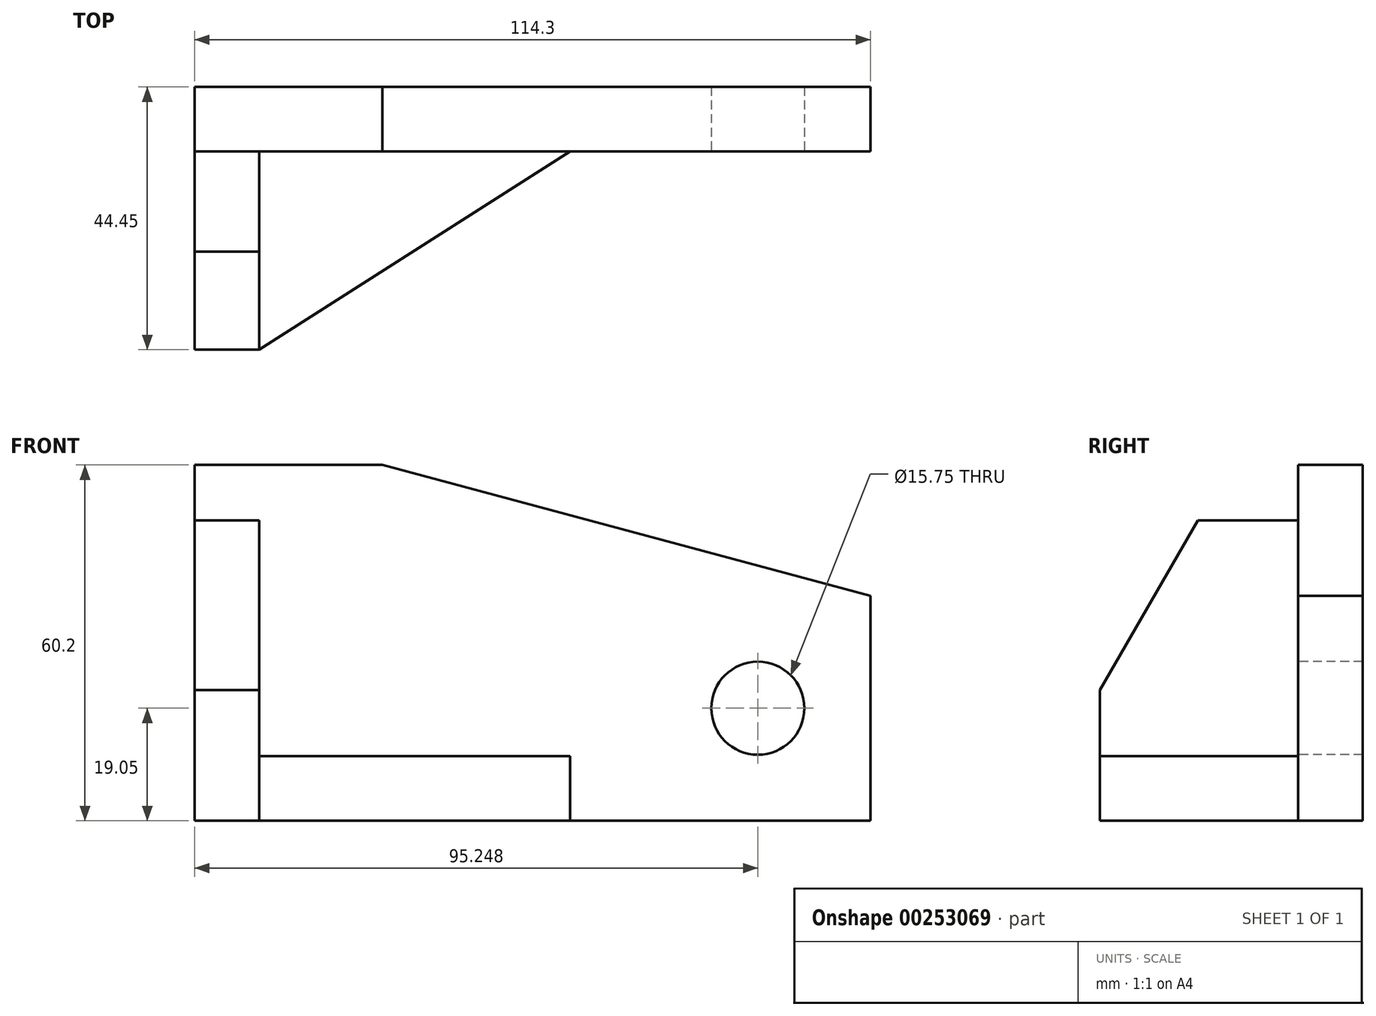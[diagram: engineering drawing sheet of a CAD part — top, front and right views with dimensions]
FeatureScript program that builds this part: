
annotation { "Feature Type Name" : "Feature", "Feature Type Description" : "" }
export const myFeature = defineFeature(function(context is Context, id is Id, definition is map)
    precondition{}
    {
        {
            var Q0;
            Q0=qCreatedBy(makeId("Front.planeOp"),FACE);
            var sketch = newSketch(context, id + "F0", { "sketchPlane" : qUnion([Q0])});
            skLineSegment(sketch, "E0.bottom", {"start": v(-10.92, 60.2) * mm, "end": v(20.83, 60.2) * mm});
            skLineSegment(sketch, "E0.top", {"start": v(-10.92, 0) * mm, "end": v(20.83, 0) * mm});
            skLineSegment(sketch, "E0.left", {"start": v(-10.92, 60.2) * mm, "end": v(-10.92, 0) * mm});
            skLineSegment(sketch, "E1", {"start": v(20.83, 60.2) * mm, "end": v(103.38, 38.08) * mm});
            skLineSegment(sketch, "E2", {"start": v(20.83, 0) * mm, "end": v(103.38, 0) * mm});
            skLineSegment(sketch, "E3", {"start": v(103.38, 38.08) * mm, "end": v(103.38, 0) * mm});
            skSolve(sketch);
        }
        {
            var Q0;
            Q0=qSketchRegion(id+"F0",true);
            extrude(context, id + "F1", {"entities" : qUnion([Q0]), "oppositeDirection" : true, "depth" : 10.92 * mm});
        }
        {
            var Q0;
            Q0=qCreatedBy(makeId("Right.planeOp"),FACE);
            var sketch = newSketch(context, id + "F2", { "sketchPlane" : qUnion([Q0])});
            skLineSegment(sketch, "E4", {"start": v(0, 0) * mm, "end": v(0, 50.8) * mm});
            skLineSegment(sketch, "E5", {"start": v(0, 50.8) * mm, "end": v(-16.96, 50.8) * mm});
            skLineSegment(sketch, "E6", {"start": v(-33.53, 22.1) * mm, "end": v(-16.96, 50.8) * mm});
            skLineSegment(sketch, "E7", {"start": v(-33.53, 22.1) * mm, "end": v(-33.53, 0) * mm});
            skLineSegment(sketch, "E8", {"start": v(-33.53, 0) * mm, "end": v(0, 0) * mm});
            skSolve(sketch);
        }
        {
            var Q0;
            Q0=makeQuery(id+"F2.imprint","IMPRINT",FACE,{"disambiguationData":[TD([[makeQuery(id+"F2.imprint","IMPRINT",EDGE,{"derivedFrom":sQuery(id+"F2.wireOp",EDGE,"E4")}),1.0]])]});
            extrude(context, id + "F3", {"entities" : qUnion([Q0]), "operationType" : NewBodyOperationType.ADD, "oppositeDirection" : true, "depth" : 10.92 * mm});
        }
        {
            var Q0;
            Q0=qCreatedBy(makeId("Top.planeOp"),FACE);
            var sketch = newSketch(context, id + "F4", { "sketchPlane" : qUnion([Q0])});
            skLineSegment(sketch, "E9", {"start": v(0, 0) * mm, "end": v(0, -33.53) * mm});
            skLineSegment(sketch, "E10", {"start": v(0, -33.53) * mm, "end": v(52.58, 0) * mm});
            skLineSegment(sketch, "E11", {"start": v(52.58, 0) * mm, "end": v(0, 0) * mm});
            skSolve(sketch);
        }
        {
            var Q0;
            Q0=qSketchRegion(id+"F4",true);
            extrude(context, id + "F5", {"entities" : qUnion([Q0]), "operationType" : NewBodyOperationType.ADD, "depth" : 10.92 * mm});
        }
        {
            var Q0;
            Q0=makeQuery(id+"F1.opExtrude","CAP_FACE",FACE,{"disambiguationData":[OSD([sQuery(id+"F0.wireOp",EDGE,"E0.bottom"),sQuery(id+"F0.wireOp",EDGE,"E0.top"),sQuery(id+"F0.wireOp",EDGE,"E0.left"),sQuery(id+"F0.wireOp",EDGE,"E1"),sQuery(id+"F0.wireOp",EDGE,"E2"),sQuery(id+"F0.wireOp",EDGE,"E3")])],"isStart":true});
            var sketch = newSketch(context, id + "F6", { "sketchPlane" : qUnion([Q0])});
            skCircle(sketch, "E12", {"center": v(84.33, 19.05) * mm, "radius": 7.87 * mm});
            skSolve(sketch);
        }
        {
            var Q0;
            Q0=qSketchRegion(id+"F6",true);
            extrude(context, id + "F7", {"entities" : qUnion([Q0]), "operationType" : NewBodyOperationType.REMOVE, "endBound" : BoundingType.THROUGH_ALL, "oppositeDirection" : true, "depth" : 25.4 * mm});
        }
    });
